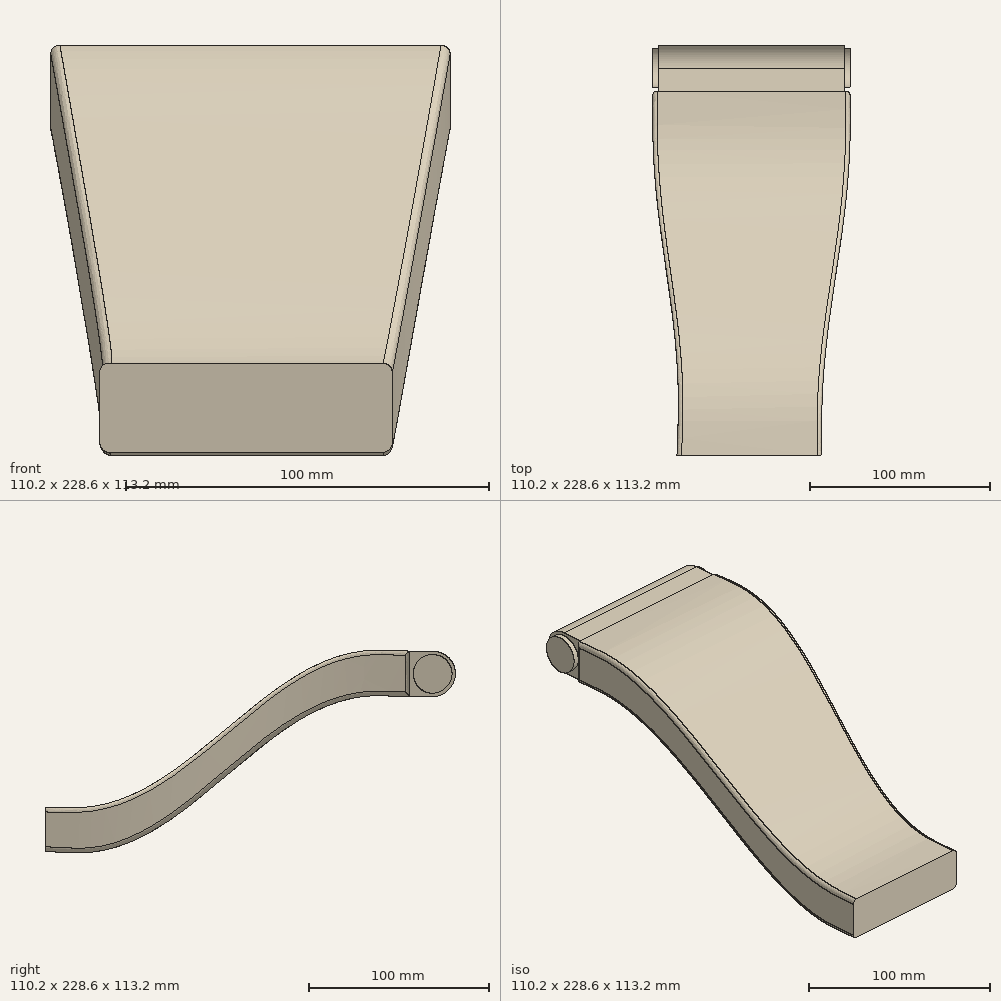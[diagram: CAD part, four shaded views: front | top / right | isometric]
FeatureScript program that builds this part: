
annotation { "Feature Type Name" : "Feature", "Feature Type Description" : "" }
export const myFeature = defineFeature(function(context is Context, id is Id, definition is map)
    precondition{}
    {
        {
            var Q0;
            Q0=qCreatedBy(makeId("Front.planeOp"),FACE);
            var sketch = newSketch(context, id + "F0", { "sketchPlane" : qUnion([Q0])});
            skLineSegment(sketch, "E0.bottom", {"start": v(-55.12, 10.6) * mm, "end": v(54.88, 10.6) * mm});
            skLineSegment(sketch, "E0.top", {"start": v(-55.12, -14.8) * mm, "end": v(54.88, -14.8) * mm});
            skLineSegment(sketch, "E0.left", {"start": v(-55.12, 10.6) * mm, "end": v(-55.12, -14.8) * mm});
            skLineSegment(sketch, "E0.right", {"start": v(54.88, 10.6) * mm, "end": v(54.88, -14.8) * mm});
            skSolve(sketch);
        }
        {
            var Q0;
            Q0=qCreatedBy(makeId("Front.planeOp"),FACE);
            cPlane(context, id + "F1", {"entities" : qUnion([Q0]), "cplaneType" : CPlaneType.OFFSET, "offset" : 25.4 * mm, "width" : 152.4 * mm, "height" : 152.4 * mm});
        }
        {
            var Q0;
            Q0=qCreatedBy(id+"F1.planeOp",FACE);
            var sketch = newSketch(context, id + "F2", { "sketchPlane" : qUnion([Q0])});
            skLineSegment(sketch, "E1.bottom", {"start": v(-55.12, 10.74) * mm, "end": v(54.88, 10.74) * mm});
            skLineSegment(sketch, "E1.top", {"start": v(-55.12, -14.66) * mm, "end": v(54.88, -14.66) * mm});
            skLineSegment(sketch, "E1.left", {"start": v(-55.12, 10.74) * mm, "end": v(-55.12, -14.66) * mm});
            skLineSegment(sketch, "E1.right", {"start": v(54.88, 10.74) * mm, "end": v(54.88, -14.66) * mm});
            skSolve(sketch);
        }
        {
            var Q0;
            Q0=qCreatedBy(id+"F1.planeOp",FACE);
            cPlane(context, id + "F3", {"entities" : qUnion([Q0]), "cplaneType" : CPlaneType.OFFSET, "offset" : 152.4 * mm, "width" : 152.4 * mm, "height" : 152.4 * mm});
        }
        {
            var Q0;
            Q0=qCreatedBy(id+"F3.planeOp",FACE);
            var sketch = newSketch(context, id + "F4", { "sketchPlane" : qUnion([Q0])});
            skLineSegment(sketch, "E2.bottom", {"start": v(-40.9, -76.16) * mm, "end": v(39.1, -76.16) * mm});
            skLineSegment(sketch, "E2.top", {"start": v(-40.9, -101.56) * mm, "end": v(39.1, -101.56) * mm});
            skLineSegment(sketch, "E2.left", {"start": v(-40.9, -76.16) * mm, "end": v(-40.9, -101.56) * mm});
            skLineSegment(sketch, "E2.right", {"start": v(39.1, -76.16) * mm, "end": v(39.1, -101.56) * mm});
            skSolve(sketch);
        }
        {
            var Q0;
            Q0=qCreatedBy(id+"F3.planeOp",FACE);
            cPlane(context, id + "F5", {"entities" : qUnion([Q0]), "cplaneType" : CPlaneType.OFFSET, "offset" : 25.4 * mm, "width" : 152.4 * mm, "height" : 152.4 * mm});
        }
        {
            var Q0;
            Q0=qCreatedBy(id+"F5.planeOp",FACE);
            var sketch = newSketch(context, id + "F6", { "sketchPlane" : qUnion([Q0])});
            skLineSegment(sketch, "E3.bottom", {"start": v(39, -76.53) * mm, "end": v(-41.68, -76.53) * mm});
            skLineSegment(sketch, "E3.top", {"start": v(39, -101.02) * mm, "end": v(-41.68, -101.02) * mm});
            skLineSegment(sketch, "E3.left", {"start": v(39, -76.53) * mm, "end": v(39, -101.02) * mm});
            skLineSegment(sketch, "E3.right", {"start": v(-41.68, -76.53) * mm, "end": v(-41.68, -101.02) * mm});
            skSolve(sketch);
        }
        {
            var Q0;
            Q0 = qSketchRegion(id + "F0", true);
            var Q1;
            Q1=makeQuery(id+"F2.imprint","IMPRINT",FACE,{"disambiguationData":[TD([[makeQuery(id+"F2.imprint","IMPRINT",EDGE,{"derivedFrom":sQuery(id+"F2.wireOp",EDGE,"E1.bottom")}),-1.0]])]});
            var Q2;
            Q2 = qSketchRegion(id + "F4", true);
            var Q3;
            Q3 = qSketchRegion(id + "F6", true);
            loft(context, id + "F7", {"sheetProfilesArray" : [{ "sheetProfileEntities" : qUnion([Q0]) }, { "sheetProfileEntities" : qUnion([Q1]) }, { "sheetProfileEntities" : qUnion([Q2]) }, { "sheetProfileEntities" : qUnion([Q3]) }]});
        }
        {
            var Q0;
            Q0=makeQuery(id+"F7.opLoft","CAP_FACE",FACE,{"disambiguationData":[OSD([makeQuery(id+"F0.imprint","IMPRINT",FACE,{"disambiguationData":[TD([[makeQuery(id+"F0.imprint","IMPRINT",EDGE,{"derivedFrom":sQuery(id+"F0.wireOp",EDGE,"E0.bottom")}),-1.0]])]})])],"isStart":true});
            var sketch = newSketch(context, id + "F8", { "sketchPlane" : qUnion([Q0])});
            skLineSegment(sketch, "E4.0", {"start": v(-54.88, -14.8) * mm, "end": v(-54.88, 10.6) * mm});
            skLineSegment(sketch, "E5.0", {"start": v(55.12, 10.6) * mm, "end": v(55.12, -14.8) * mm});
            skLineSegment(sketch, "E6.bottom", {"start": v(-54.88, 10.6) * mm, "end": v(-51.58, 10.6) * mm});
            skLineSegment(sketch, "E6.top", {"start": v(-54.88, -14.8) * mm, "end": v(-51.58, -14.8) * mm});
            skLineSegment(sketch, "E6.left", {"start": v(-54.88, 10.6) * mm, "end": v(-54.88, -14.8) * mm});
            skLineSegment(sketch, "E6.right", {"start": v(-51.58, 10.6) * mm, "end": v(-51.58, -14.8) * mm});
            skLineSegment(sketch, "E7.bottom", {"start": v(55.12, 10.6) * mm, "end": v(51.82, 10.6) * mm});
            skLineSegment(sketch, "E7.top", {"start": v(55.12, -14.8) * mm, "end": v(51.82, -14.8) * mm});
            skLineSegment(sketch, "E7.right", {"start": v(51.82, 10.6) * mm, "end": v(51.82, -14.8) * mm});
            skSolve(sketch);
        }
        {
            var Q0;
            {var subQ0=sQuery(id+"F8.wireOp",EDGE,"E6.right");Q0=makeQuery(id+"F8.imprint","IMPRINT",FACE,{"disambiguationData":[TD([[makeQuery(id+"F8.imprint","IMPRINT",EDGE,{"derivedFrom":subQ0}),1.0]])]});}
            extrude(context, id + "F9", {"entities" : qUnion([Q0]), "operationType" : NewBodyOperationType.ADD, "depth" : 25.4 * mm});
        }
        {
            var Q0;
            Q0=makeQuery(id+"F9.opExtrude","SWEPT_FACE",FACE,{"disambiguationData":[OSD([sQuery(id+"F8.wireOp",EDGE,"E6.right")])]});
            var sketch = newSketch(context, id + "F10", { "sketchPlane" : qUnion([Q0])});
            skCircle(sketch, "E8", {"center": v(12.7, -2.1) * mm, "radius": 10.8 * mm});
            skPoint(sketch, "E8.centerSnap0", {"position": v(25.4, -2.1) * mm});
            skPoint(sketch, "E8.centerSnap1", {"position": v(12.7, -14.8) * mm});
            skSolve(sketch);
        }
        {
            var Q0;
            Q0=makeQuery(id+"F9.opExtrude","SWEPT_FACE",FACE,{"disambiguationData":[OSD([sQuery(id+"F8.wireOp",EDGE,"E7.right")])]});
            var sketch = newSketch(context, id + "F11", { "sketchPlane" : qUnion([Q0])});
            skCircle(sketch, "E9", {"center": v(-12.7, -2.1) * mm, "radius": 10.8 * mm});
            skPoint(sketch, "E9.centerSnap0", {"position": v(-12.7, -14.8) * mm});
            skPoint(sketch, "E9.centerSnap1", {"position": v(-25.4, -2.1) * mm});
            skSolve(sketch);
        }
        {
            var Q0;
            Q0 = qSketchRegion(id + "F11", true);
            var Q1;
            Q1=makeQuery(id+"F10.imprint","IMPRINT",FACE,{"disambiguationData":[TD([[makeQuery(id+"F10.imprint","IMPRINT",EDGE,{"derivedFrom":sQuery(id+"F10.wireOp",EDGE,"E8")}),1.0]])]});
            extrude(context, id + "F12", {"entities" : qUnion([Q0, Q1]), "operationType" : NewBodyOperationType.ADD, "depth" : 3.3 * mm, "hasSecondDirection" : true, "secondDirectionOppositeDirection" : true, "secondDirectionDepth" : 3.3 * mm});
        }
        {
            var Q0;
            Q0=makeQuery(id+"F9.opExtrude","CAP_EDGE",EDGE,{"disambiguationData":[OSD([sQuery(id+"F0.wireOp",EDGE,"E0.bottom"),sQuery(id+"F0.wireOp",EDGE,"E0.left"),sQuery(id+"F0.wireOp",EDGE,"E0.right")])],"isStart":false});
            var Q1;
            Q1=makeQuery(id+"F9.opExtrude","CAP_EDGE",EDGE,{"disambiguationData":[OSD([sQuery(id+"F0.wireOp",EDGE,"E0.top"),sQuery(id+"F0.wireOp",EDGE,"E0.left"),sQuery(id+"F0.wireOp",EDGE,"E0.right")])],"isStart":false});
            fillet(context, id + "F13", {"entities" : qUnion([Q0, Q1]), "radius" : 12.7 * mm, "tangentPropagation" : true, "allowEdgeOverflow" : false});
        }
        {
            var Q0;
            Q0=makeQuery(id+"F7.opLoft","SWEPT_EDGE",EDGE,{"disambiguationData":[OSD([sQuery(id+"F0.wireOp",EDGE,"E0.bottom"),sQuery(id+"F0.wireOp",EDGE,"E0.right"),sQuery(id+"F2.wireOp",EDGE,"E1.bottom"),sQuery(id+"F2.wireOp",EDGE,"E1.right")])]});
            var Q1;
            Q1=makeQuery(id+"F7.opLoft","SWEPT_EDGE",EDGE,{"disambiguationData":[OSD([sQuery(id+"F0.wireOp",EDGE,"E0.top"),sQuery(id+"F0.wireOp",EDGE,"E0.right"),sQuery(id+"F2.wireOp",EDGE,"E1.top"),sQuery(id+"F2.wireOp",EDGE,"E1.right")])]});
            var Q2;
            Q2=makeQuery(id+"F7.opLoft","SWEPT_EDGE",EDGE,{"disambiguationData":[OSD([sQuery(id+"F0.wireOp",EDGE,"E0.bottom"),sQuery(id+"F0.wireOp",EDGE,"E0.left"),sQuery(id+"F2.wireOp",EDGE,"E1.bottom"),sQuery(id+"F2.wireOp",EDGE,"E1.left")])]});
            var Q3;
            Q3=makeQuery(id+"F7.opLoft","SWEPT_EDGE",EDGE,{"disambiguationData":[OSD([sQuery(id+"F0.wireOp",EDGE,"E0.top"),sQuery(id+"F0.wireOp",EDGE,"E0.left"),sQuery(id+"F2.wireOp",EDGE,"E1.top"),sQuery(id+"F2.wireOp",EDGE,"E1.left")])]});
            var Q4;
            Q4=makeQuery(id+"F7.opLoft","MID_CAP_EDGE",EDGE,{"disambiguationData":[OSD([sQuery(id+"F0.wireOp",EDGE,"E0.bottom"),sQuery(id+"F0.wireOp",EDGE,"E0.top"),sQuery(id+"F0.wireOp",EDGE,"E0.left")])],"capPos":0.0});
            var Q5;
            Q5=makeQuery(id+"F7.opLoft","MID_CAP_EDGE",EDGE,{"disambiguationData":[OSD([sQuery(id+"F0.wireOp",EDGE,"E0.bottom"),sQuery(id+"F0.wireOp",EDGE,"E0.top"),sQuery(id+"F0.wireOp",EDGE,"E0.right")])],"capPos":0.0});
            fillet(context, id + "F14", {"entities" : qUnion([Q0, Q1, Q2, Q3, Q4, Q5]), "radius" : 2.54 * mm, "tangentPropagation" : true, "allowEdgeOverflow" : false});
        }
        {
            var Q0;
            Q0=qCreatedBy(id+"F5.planeOp",FACE);
            cPlane(context, id + "F15", {"entities" : qUnion([Q0]), "cplaneType" : CPlaneType.OFFSET, "offset" : 25.4 * mm, "width" : 152.4 * mm, "height" : 152.4 * mm});
        }
        {
            var Q0;
            Q0=qCreatedBy(makeId("Front.planeOp"),FACE);
            cPlane(context, id + "F16", {"entities" : qUnion([Q0]), "cplaneType" : CPlaneType.OFFSET, "offset" : 38.1 * mm, "oppositeDirection" : true, "width" : 152.4 * mm, "height" : 152.4 * mm});
        }
    });
